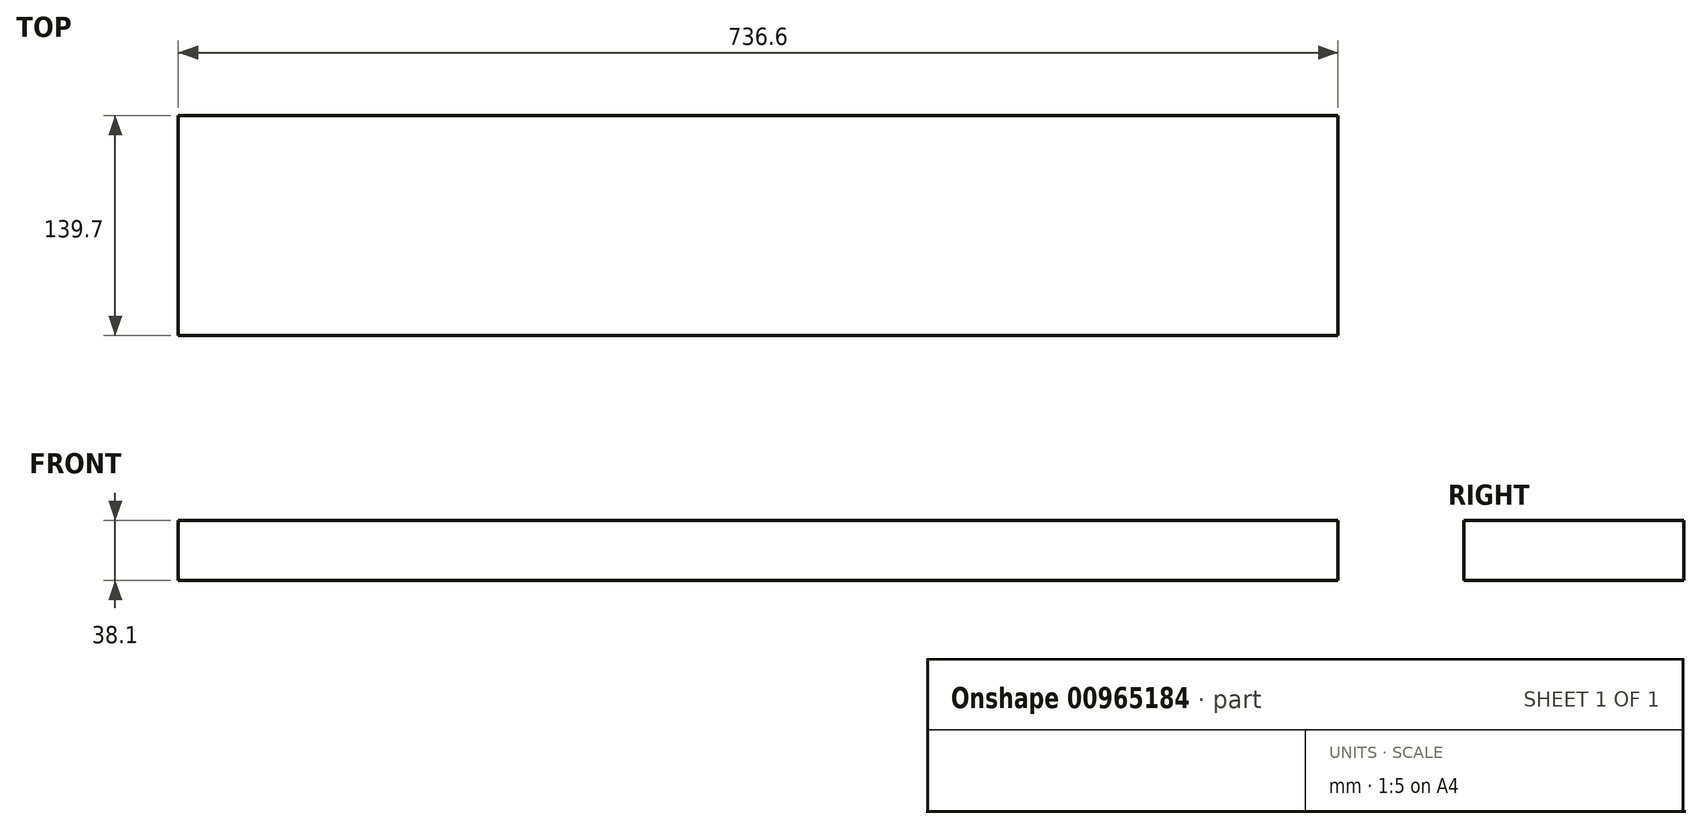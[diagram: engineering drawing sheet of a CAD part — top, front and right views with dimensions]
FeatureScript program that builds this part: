
annotation { "Feature Type Name" : "Feature", "Feature Type Description" : "" }
export const myFeature = defineFeature(function(context is Context, id is Id, definition is map)
    precondition{}
    {
        {
            var Q0;
            Q0=qCreatedBy(makeId("Right.planeOp"),FACE);
            var sketch = newSketch(context, id + "F0", { "sketchPlane" : qUnion([Q0])});
            skLineSegment(sketch, "E0.bottom", {"start": v(-29.55, -90.15) * mm, "end": v(110.15, -90.15) * mm});
            skLineSegment(sketch, "E0.top", {"start": v(-29.55, -52.05) * mm, "end": v(110.15, -52.05) * mm});
            skLineSegment(sketch, "E0.left", {"start": v(-29.55, -90.15) * mm, "end": v(-29.55, -52.05) * mm});
            skLineSegment(sketch, "E0.right", {"start": v(110.15, -90.15) * mm, "end": v(110.15, -52.05) * mm});
            skSolve(sketch);
        }
        {
            var Q0;
            Q0 = qSketchRegion(id + "F0", true);
            extrude(context, id + "F1", {"entities" : qUnion([Q0]), "depth" : 736.6 * mm, "offsetDistance" : 25.4 * mm});
        }
    });
